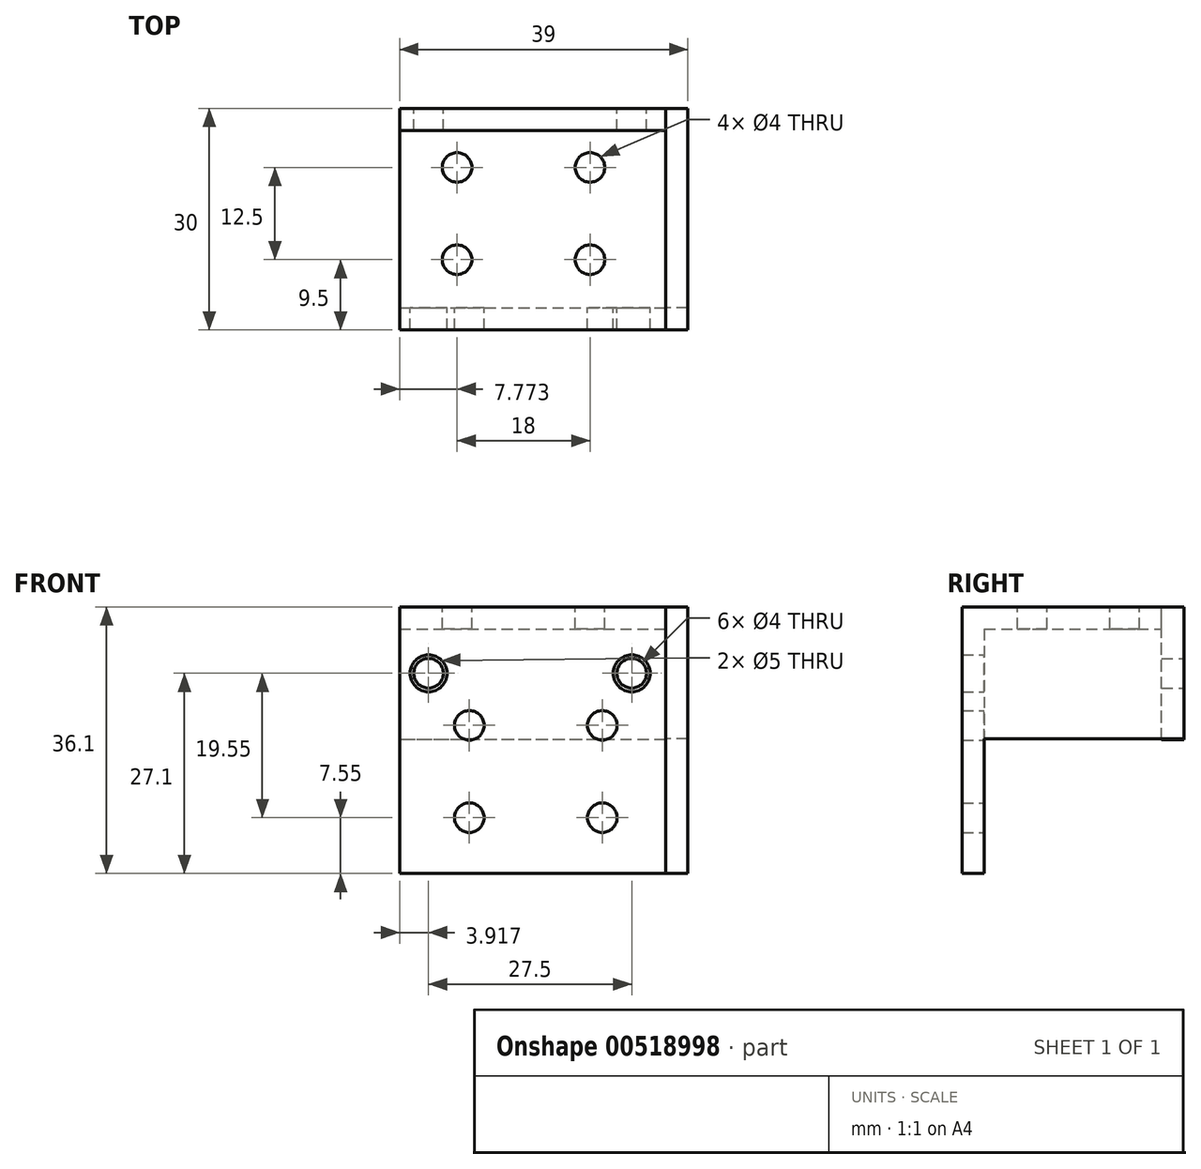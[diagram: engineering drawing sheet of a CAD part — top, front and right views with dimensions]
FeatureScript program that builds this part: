
annotation { "Feature Type Name" : "Feature", "Feature Type Description" : "" }
export const myFeature = defineFeature(function(context is Context, id is Id, definition is map)
    precondition{}
    {
        {
            var Q0;
            Q0=qCreatedBy(makeId("Front.planeOp"),FACE);
            var sketch = newSketch(context, id + "F0", { "sketchPlane" : qUnion([Q0])});
            skLineSegment(sketch, "E0.bottom", {"start": v(18, -9) * mm, "end": v(-18, -9) * mm});
            skLineSegment(sketch, "E0.top", {"start": v(18, 9) * mm, "end": v(-18, 9) * mm});
            skLineSegment(sketch, "E0.left", {"start": v(18, -9) * mm, "end": v(18, 9) * mm});
            skLineSegment(sketch, "E0.right", {"start": v(-18, -9) * mm, "end": v(-18, 9) * mm});
            skPoint(sketch, "E0.middle", {"position": v(0, 0) * mm});
            skCircle(sketch, "E1", {"center": v(-14.08, 0) * mm, "radius": 2 * mm});
            skCircle(sketch, "E2", {"center": v(13.42, 0) * mm, "radius": 2 * mm});
            skLineSegment(sketch, "E3", {"start": v(-14.08, 0) * mm, "end": v(13.42, 0) * mm, "construction": true});
            skSolve(sketch);
        }
        {
            var Q0;
            Q0=makeQuery(id+"F0.imprint","IMPRINT",FACE,{"disambiguationData":[TD([[makeQuery(id+"F0.imprint","IMPRINT",EDGE,{"derivedFrom":sQuery(id+"F0.wireOp",EDGE,"E0.bottom")}),-1.0]])]});
            extrude(context, id + "F1", {"entities" : qUnion([Q0]), "depth" : 3 * mm, "offsetDistance" : 25 * mm});
        }
        {
            var Q0;
            Q0=makeQuery(id+"F1.opExtrude","CAP_FACE",FACE,{"disambiguationData":[OSD([sQuery(id+"F0.wireOp",EDGE,"E0.bottom"),sQuery(id+"F0.wireOp",EDGE,"E0.top"),sQuery(id+"F0.wireOp",EDGE,"E0.left"),sQuery(id+"F0.wireOp",EDGE,"E0.right"),sQuery(id+"F0.wireOp",EDGE,"E1"),sQuery(id+"F0.wireOp",EDGE,"E2")])],"isStart":false});
            var sketch = newSketch(context, id + "F2", { "sketchPlane" : qUnion([Q0])});
            skLineSegment(sketch, "E4.bottom", {"start": v(-18, 9) * mm, "end": v(18, 9) * mm});
            skLineSegment(sketch, "E4.top", {"start": v(-18, 6) * mm, "end": v(18, 6) * mm});
            skLineSegment(sketch, "E4.left", {"start": v(-18, 9) * mm, "end": v(-18, 6) * mm});
            skLineSegment(sketch, "E4.right", {"start": v(18, 9) * mm, "end": v(18, 6) * mm});
            skSolve(sketch);
        }
        {
            var Q0;
            Q0 = qSketchRegion(id + "F2", true);
            extrude(context, id + "F3", {"entities" : qUnion([Q0]), "depth" : 24 * mm, "offsetDistance" : 25 * mm});
        }
        {
            var Q0;
            Q0=makeQuery(id+"F3.opExtrude","SWEPT_FACE",FACE,{"disambiguationData":[OSD([sQuery(id+"F2.wireOp",EDGE,"E4.bottom")])]});
            var sketch = newSketch(context, id + "F4", { "sketchPlane" : qUnion([Q0])});
            skLineSegment(sketch, "E5", {"start": v(0, 0) * mm, "end": v(0, -8) * mm, "construction": true});
            skLineSegment(sketch, "E6", {"start": v(0, -8) * mm, "end": v(-18, -8) * mm, "construction": true});
            skCircle(sketch, "E7", {"center": v(-10.23, -8) * mm, "radius": 2 * mm});
            skCircle(sketch, "E8", {"center": v(-10.23, -20.5) * mm, "radius": 2 * mm});
            skCircle(sketch, "E9", {"center": v(7.77, -20.5) * mm, "radius": 2 * mm});
            skCircle(sketch, "E10", {"center": v(7.77, -8) * mm, "radius": 2 * mm});
            skSolve(sketch);
        }
        {
            var Q0;
            Q0 = qSketchRegion(id + "F4", true);
            extrude(context, id + "F5", {"entities" : qUnion([Q0]), "operationType" : NewBodyOperationType.REMOVE, "oppositeDirection" : true, "depth" : 25 * mm, "offsetDistance" : 25 * mm});
        }
        {
            var Q0;
            Q0=makeQuery(id+"F3.opExtrude","CAP_FACE",FACE,{"disambiguationData":[OSD([sQuery(id+"F2.wireOp",EDGE,"E4.bottom"),sQuery(id+"F2.wireOp",EDGE,"E4.top"),sQuery(id+"F2.wireOp",EDGE,"E4.left"),sQuery(id+"F2.wireOp",EDGE,"E4.right")])],"isStart":false});
            var sketch = newSketch(context, id + "F6", { "sketchPlane" : qUnion([Q0])});
            skPoint(sketch, "E11.oppositeSnap0", {"position": v(18, 7.5) * mm});
            skLineSegment(sketch, "E11.bottom", {"start": v(-18, 9) * mm, "end": v(18, 9) * mm});
            skLineSegment(sketch, "E11.top", {"start": v(-18, -27.1) * mm, "end": v(18, -27.1) * mm});
            skLineSegment(sketch, "E11.left", {"start": v(-18, 9) * mm, "end": v(-18, -27.1) * mm});
            skLineSegment(sketch, "E11.right", {"start": v(18, 9) * mm, "end": v(18, -27.1) * mm});
            skCircle(sketch, "E12", {"center": v(-8.57, -7.05) * mm, "radius": 2 * mm});
            skCircle(sketch, "E13", {"center": v(9.43, -7.05) * mm, "radius": 2 * mm});
            skCircle(sketch, "E14", {"center": v(9.43, -19.55) * mm, "radius": 2 * mm});
            skCircle(sketch, "E15", {"center": v(-8.57, -19.55) * mm, "radius": 2 * mm});
            skCircle(sketch, "E16", {"center": v(-14.08, 0) * mm, "radius": 2.5 * mm});
            skCircle(sketch, "E17", {"center": v(13.42, 0) * mm, "radius": 2.5 * mm});
            skSolve(sketch);
        }
        {
            var Q0;
            {var subQ2=sQuery(id+"F6.wireOp",EDGE,"E11.top");Q0=makeQuery(id+"F6.imprint","IMPRINT",FACE,{"disambiguationData":[TD([[makeQuery(id+"F6.imprint","IMPRINT",EDGE,{"derivedFrom":subQ2}),1.0]])]});}
            var Q1;
            {var subQ0=sQuery(id+"F6.wireOp",EDGE,"E11.bottom");Q1=makeQuery(id+"F6.imprint","IMPRINT",FACE,{"disambiguationData":[TD([[makeQuery(id+"F6.imprint","IMPRINT",EDGE,{"derivedFrom":subQ0}),1.0]])]});}
            extrude(context, id + "F7", {"entities" : qUnion([Q0, Q1]), "operationType" : NewBodyOperationType.ADD, "depth" : 3 * mm, "offsetDistance" : 25 * mm});
        }
        {
            var Q0;
            Q0=makeQuery(id+"F7.boolean.opBoolean","MERGE",FACE,{"derivedFrom":[makeQuery(id+"F3.opExtrude","SWEPT_FACE",FACE,{"disambiguationData":[OSD([sQuery(id+"F2.wireOp",EDGE,"E4.right")])]}),makeQuery(id+"F7.opExtrude","SWEPT_FACE",FACE,{"disambiguationData":[OSD([sQuery(id+"F6.wireOp",EDGE,"E11.right")])]})]});
            var sketch = newSketch(context, id + "F8", { "sketchPlane" : qUnion([Q0])});
            skLineSegment(sketch, "E18", {"start": v(-30, -27.1) * mm, "end": v(-30, 9) * mm});
            skLineSegment(sketch, "E19", {"start": v(-30, 9) * mm, "end": v(0, 9) * mm});
            skLineSegment(sketch, "E20", {"start": v(0, 9) * mm, "end": v(0, -8.87) * mm});
            skLineSegment(sketch, "E21", {"start": v(0, -8.87) * mm, "end": v(-3, -8.87) * mm});
            skLineSegment(sketch, "E22", {"start": v(-3, -8.87) * mm, "end": v(-27, -8.87) * mm});
            skLineSegment(sketch, "E23", {"start": v(-27, -8.87) * mm, "end": v(-27, -27.1) * mm});
            skSolve(sketch);
        }
        {
            var Q0;
            {var subQ1=sQuery(id+"F8.wireOp",EDGE,"E20");Q0=makeQuery(id+"F8.imprint","IMPRINT",FACE,{"disambiguationData":[TD([[makeQuery(id+"F8.imprint","IMPRINT",EDGE,{"derivedFrom":subQ1}),-1.0]])]});}
            var Q1;
            {var subQ5=sQuery(id+"F8.wireOp",EDGE,"E18");Q1=makeQuery(id+"F8.imprint","IMPRINT",FACE,{"disambiguationData":[TD([[makeQuery(id+"F8.imprint","IMPRINT",EDGE,{"derivedFrom":subQ5}),1.0]])]});}
            extrude(context, id + "F9", {"entities" : qUnion([Q0, Q1]), "depth" : 3 * mm, "offsetDistance" : 25 * mm});
        }
    });
